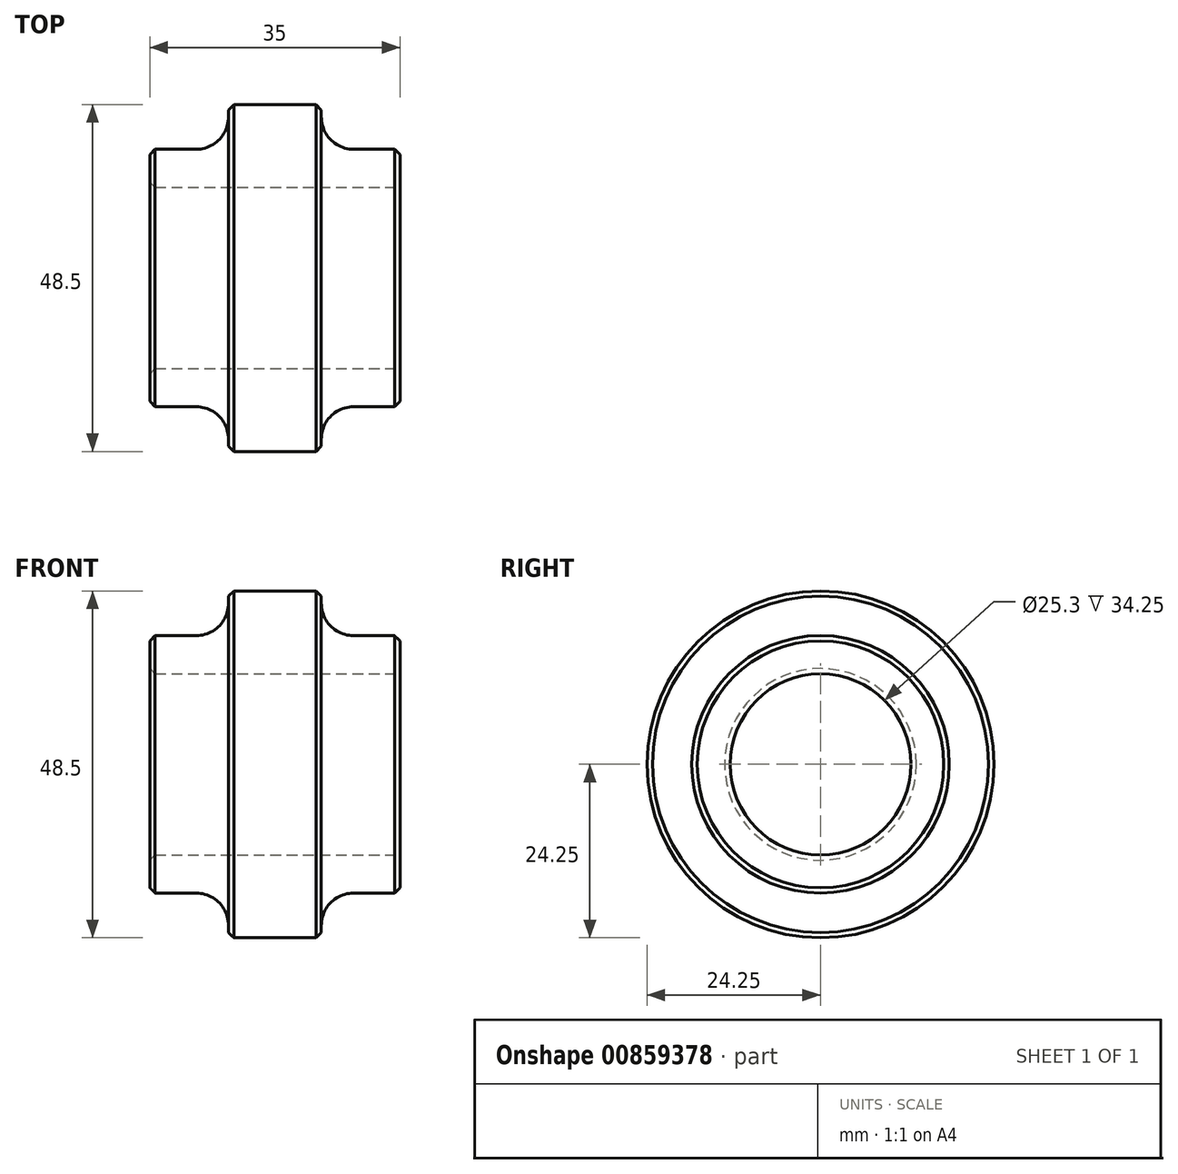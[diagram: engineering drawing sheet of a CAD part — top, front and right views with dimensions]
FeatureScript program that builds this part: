
annotation { "Feature Type Name" : "Feature", "Feature Type Description" : "" }
export const myFeature = defineFeature(function(context is Context, id is Id, definition is map)
    precondition{}
    {
        {
            var Q0;
            Q0=qCreatedBy(makeId("Front.planeOp"),FACE);
            var sketch = newSketch(context, id + "F0", { "sketchPlane" : qUnion([Q0])});
            skLineSegment(sketch, "E0", {"start": v(0, 0) * mm, "end": v(17.5, 0) * mm});
            skLineSegment(sketch, "E1", {"start": v(0, 0) * mm, "end": v(-17.5, 0) * mm});
            skLineSegment(sketch, "E2", {"start": v(-17.5, 0) * mm, "end": v(-17.5, 18) * mm});
            skLineSegment(sketch, "E3", {"start": v(-17.5, 18) * mm, "end": v(-6.5, 18) * mm});
            skLineSegment(sketch, "E4", {"start": v(-6.5, 18) * mm, "end": v(-6.5, 24.25) * mm});
            skLineSegment(sketch, "E5", {"start": v(-6.5, 24.25) * mm, "end": v(6.5, 24.25) * mm});
            skLineSegment(sketch, "E6", {"start": v(6.5, 24.25) * mm, "end": v(6.5, 18) * mm});
            skLineSegment(sketch, "E7", {"start": v(6.5, 18) * mm, "end": v(17.5, 18) * mm});
            skLineSegment(sketch, "E8", {"start": v(17.5, 18) * mm, "end": v(17.5, 0) * mm});
            skSolve(sketch);
        }
        {
            var Q0;
            Q0=makeQuery(id+"F0.imprint","IMPRINT",FACE,{"disambiguationData":[TD([[makeQuery(id+"F0.imprint","IMPRINT",EDGE,{"derivedFrom":sQuery(id+"F0.wireOp",EDGE,"E0")}),1.0]])]});
            var Q1;
            Q1=sQuery(id+"F0.wireOp",EDGE,"E1");
            revolve(context, id + "F1", {"surfaceOperationType" : NewSurfaceOperationType.NEW, "entities" : qUnion([Q0]), "axis" : qUnion([Q1]), "revolveType" : RevolveType.FULL});
        }
        {
            var Q0;
            Q0=makeQuery(id+"F1.opRevolve","SWEPT_EDGE",EDGE,{"disambiguationData":[OSD([sQuery(id+"F0.wireOp",EDGE,"E6"),sQuery(id+"F0.wireOp",EDGE,"E7")])]});
            var Q1;
            Q1=makeQuery(id+"F1.opRevolve","SWEPT_EDGE",EDGE,{"disambiguationData":[OSD([sQuery(id+"F0.wireOp",EDGE,"E3"),sQuery(id+"F0.wireOp",EDGE,"E4")])]});
            fillet(context, id + "F2", {"entities" : qUnion([Q0, Q1]), "radius" : 4.5 * mm, "tangentPropagation" : true, "allowEdgeOverflow" : false});
        }
        {
            var Q0;
            Q0=makeQuery(id+"F1.opRevolve","SWEPT_FACE",FACE,{"disambiguationData":[OSD([sQuery(id+"F0.wireOp",EDGE,"E8")])]});
            var sketch = newSketch(context, id + "F3", { "sketchPlane" : qUnion([Q0])});
            skCircle(sketch, "E9", {"center": v(0, 0) * mm, "radius": 12.65 * mm});
            skSolve(sketch);
        }
        {
            var Q0;
            Q0=makeQuery(id+"F3.imprint","IMPRINT",FACE,{"disambiguationData":[TD([[makeQuery(id+"F3.imprint","IMPRINT",EDGE,{"derivedFrom":sQuery(id+"F3.wireOp",EDGE,"E9")}),1.0]])]});
            extrude(context, id + "F4", {"entities" : qUnion([Q0]), "operationType" : NewBodyOperationType.REMOVE, "endBound" : BoundingType.THROUGH_ALL, "oppositeDirection" : true, "depth" : 52.1 * mm, "offsetDistance" : 25 * mm});
        }
        {
            var Q0;
            Q0=makeQuery(id+"F4.boolean.opBoolean","COPY",EDGE,{"derivedFrom":makeQuery(id+"F4.opExtrude","CAP_EDGE",EDGE,{"disambiguationData":[OSD([sQuery(id+"F3.wireOp",EDGE,"E9")])],"isStart":true})});
            var Q1;
            Q1=makeQuery(id+"F4.boolean.opBoolean","INTERSECT",EDGE,{"derivedFrom":[makeQuery(id+"F1.opRevolve","SWEPT_FACE",FACE,{"disambiguationData":[OSD([sQuery(id+"F0.wireOp",EDGE,"E2")])]}),makeQuery(id+"F4.opExtrude","SWEPT_FACE",FACE,{"disambiguationData":[OSD([sQuery(id+"F3.wireOp",EDGE,"E9")])]})]});
            var Q2;
            Q2=makeQuery(id+"F1.opRevolve","SWEPT_EDGE",EDGE,{"disambiguationData":[OSD([sQuery(id+"F0.wireOp",EDGE,"E4"),sQuery(id+"F0.wireOp",EDGE,"E5")])]});
            var Q3;
            Q3=makeQuery(id+"F1.opRevolve","SWEPT_EDGE",EDGE,{"disambiguationData":[OSD([sQuery(id+"F0.wireOp",EDGE,"E2"),sQuery(id+"F0.wireOp",EDGE,"E3")])]});
            var Q4;
            Q4=makeQuery(id+"F1.opRevolve","SWEPT_EDGE",EDGE,{"disambiguationData":[OSD([sQuery(id+"F0.wireOp",EDGE,"E5"),sQuery(id+"F0.wireOp",EDGE,"E6")])]});
            var Q5;
            Q5=makeQuery(id+"F1.opRevolve","SWEPT_EDGE",EDGE,{"disambiguationData":[OSD([sQuery(id+"F0.wireOp",EDGE,"E7"),sQuery(id+"F0.wireOp",EDGE,"E8")])]});
            chamfer(context, id + "F5", {"entities" : qUnion([Q0, Q1, Q2, Q3, Q4, Q5]), "width" : 0.75 * mm, "tangentPropagation" : true});
        }
    });
